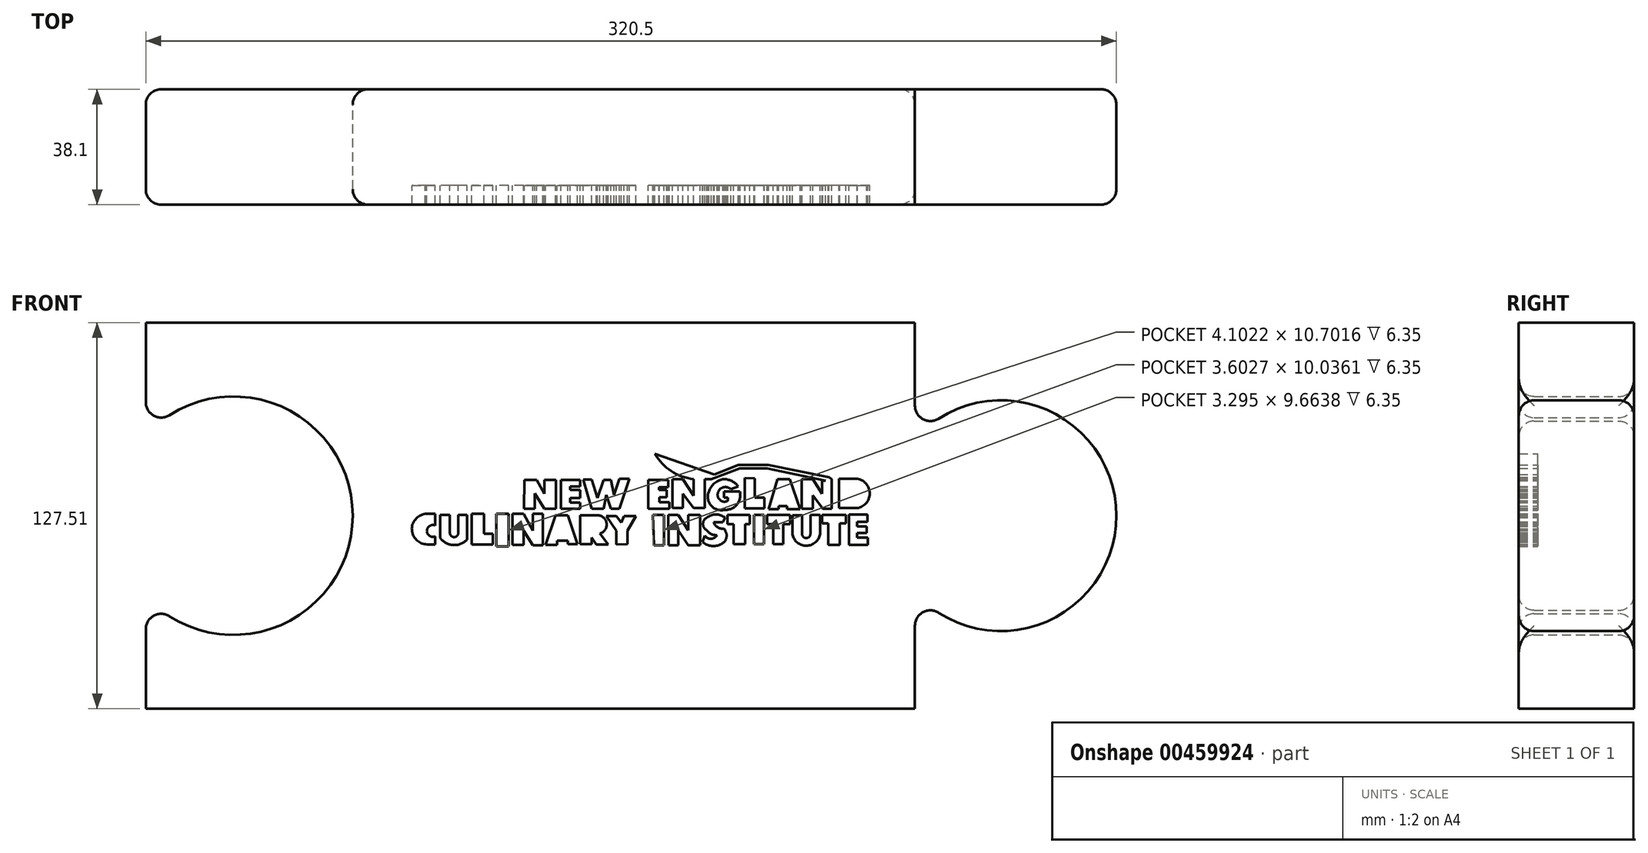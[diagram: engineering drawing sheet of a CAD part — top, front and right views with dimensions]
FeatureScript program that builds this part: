
annotation { "Feature Type Name" : "Feature", "Feature Type Description" : "" }
export const myFeature = defineFeature(function(context is Context, id is Id, definition is map)
    precondition{}
    {
        {
            var Q0;
            Q0=qCreatedBy(makeId("Front.planeOp"),FACE);
            var sketch = newSketch(context, id + "F0", { "sketchPlane" : qUnion([Q0])});
            skLineSegment(sketch, "E0", {"start": v(-171.41, 87.34) * mm, "end": v(82.59, 87.34) * mm});
            skLineSegment(sketch, "E1", {"start": v(-171.41, -40.17) * mm, "end": v(82.59, -40.17) * mm});
            skArc(sketch, "E2", {"start": v(82.59, -1.81) * mm, "mid": v(149.09, 23.59) * mm, "end": v(82.59, 48.99) * mm});
            skLineSegment(sketch, "E3", {"start": v(82.59, 48.99) * mm, "end": v(82.59, 87.34) * mm});
            skLineSegment(sketch, "E4", {"start": v(82.59, -1.81) * mm, "end": v(82.59, -40.17) * mm});
            skArc(sketch, "E5", {"start": v(-171.41, -3.08) * mm, "mid": v(-103.08, 23.59) * mm, "end": v(-171.41, 50.26) * mm});
            skLineSegment(sketch, "E6", {"start": v(-171.41, -3.08) * mm, "end": v(-171.41, -40.17) * mm});
            skLineSegment(sketch, "E7", {"start": v(-171.41, 50.26) * mm, "end": v(-171.41, 87.34) * mm});
            skLineSegment(sketch, "E8", {"start": v(-3.33, 44.08) * mm, "end": v(16.32, 37.2) * mm});
            skArc(sketch, "E9", {"start": v(-3.33, 44.08) * mm, "mid": v(2.1, 38.34) * mm, "end": v(9.53, 35.67) * mm});
            skLineSegment(sketch, "E10", {"start": v(9.53, 35.67) * mm, "end": v(9.53, 30.22) * mm});
            skLineSegment(sketch, "E11", {"start": v(9.53, 30.22) * mm, "end": v(5.93, 35.67) * mm});
            skLineSegment(sketch, "E12", {"start": v(5.93, 35.67) * mm, "end": v(2.47, 35.67) * mm});
            skLineSegment(sketch, "E13", {"start": v(2.47, 35.67) * mm, "end": v(2.47, 26.11) * mm});
            skLineSegment(sketch, "E14", {"start": v(2.47, 26.11) * mm, "end": v(5.93, 26.11) * mm});
            skLineSegment(sketch, "E15", {"start": v(5.93, 26.11) * mm, "end": v(5.93, 30.86) * mm});
            skLineSegment(sketch, "E16", {"start": v(5.93, 30.86) * mm, "end": v(9.53, 26.11) * mm});
            skLineSegment(sketch, "E17", {"start": v(9.53, 26.11) * mm, "end": v(13.12, 26.11) * mm});
            skLineSegment(sketch, "E18", {"start": v(13.12, 26.11) * mm, "end": v(13.12, 35.67) * mm});
            skLineSegment(sketch, "E19", {"start": v(13.12, 35.67) * mm, "end": v(15.3, 35.67) * mm});
            skLineSegment(sketch, "E20", {"start": v(16.32, 37.2) * mm, "end": v(24.18, 40.36) * mm});
            skLineSegment(sketch, "E21", {"start": v(15.3, 35.67) * mm, "end": v(24.7, 39.18) * mm});
            skLineSegment(sketch, "E22", {"start": v(24.7, 39.18) * mm, "end": v(33.7, 39.18) * mm});
            skLineSegment(sketch, "E23", {"start": v(24.18, 40.36) * mm, "end": v(34.15, 40.36) * mm});
            skLineSegment(sketch, "E24", {"start": v(33.7, 39.18) * mm, "end": v(53.02, 35.17) * mm});
            skLineSegment(sketch, "E25", {"start": v(34.15, 40.36) * mm, "end": v(54.26, 36.28) * mm});
            skLineSegment(sketch, "E26", {"start": v(53.02, 35.17) * mm, "end": v(51.9, 35.17) * mm});
            skLineSegment(sketch, "E27", {"start": v(51.9, 35.17) * mm, "end": v(51.9, 30.86) * mm});
            skLineSegment(sketch, "E28", {"start": v(51.9, 30.86) * mm, "end": v(48.82, 35.67) * mm});
            skLineSegment(sketch, "E29", {"start": v(48.82, 35.67) * mm, "end": v(45.2, 35.67) * mm});
            skLineSegment(sketch, "E30", {"start": v(45.2, 35.67) * mm, "end": v(45.2, 25.85) * mm});
            skLineSegment(sketch, "E31", {"start": v(45.2, 25.85) * mm, "end": v(48.89, 25.85) * mm});
            skLineSegment(sketch, "E32", {"start": v(48.89, 25.85) * mm, "end": v(48.89, 30.3) * mm});
            skLineSegment(sketch, "E33", {"start": v(48.89, 30.3) * mm, "end": v(52.16, 25.85) * mm});
            skLineSegment(sketch, "E34", {"start": v(52.16, 25.85) * mm, "end": v(55.07, 25.85) * mm});
            skLineSegment(sketch, "E35", {"start": v(55.07, 25.85) * mm, "end": v(55.07, 35.67) * mm});
            skLineSegment(sketch, "E36", {"start": v(54.26, 36.28) * mm, "end": v(55.07, 35.67) * mm});
            skLineSegment(sketch, "E37", {"start": v(-46.5, 25.85) * mm, "end": v(-42.9, 25.85) * mm});
            skLineSegment(sketch, "E38", {"start": v(-42.9, 25.85) * mm, "end": v(-42.9, 30.97) * mm});
            skLineSegment(sketch, "E39", {"start": v(-42.9, 30.97) * mm, "end": v(-39.72, 25.85) * mm});
            skLineSegment(sketch, "E40", {"start": v(-39.72, 25.85) * mm, "end": v(-35.95, 25.85) * mm});
            skLineSegment(sketch, "E41", {"start": v(-35.95, 25.85) * mm, "end": v(-35.95, 35.4) * mm});
            skLineSegment(sketch, "E42", {"start": v(-35.95, 35.4) * mm, "end": v(-39.72, 35.4) * mm});
            skLineSegment(sketch, "E43", {"start": v(-39.72, 35.4) * mm, "end": v(-39.72, 30.89) * mm});
            skLineSegment(sketch, "E44", {"start": v(-39.72, 30.89) * mm, "end": v(-42.33, 35.4) * mm});
            skLineSegment(sketch, "E45", {"start": v(-42.33, 35.4) * mm, "end": v(-46.4, 35.4) * mm});
            skLineSegment(sketch, "E46", {"start": v(-46.4, 35.4) * mm, "end": v(-46.5, 25.85) * mm});
            skLineSegment(sketch, "E47", {"start": v(-34.35, 35.4) * mm, "end": v(-34.35, 25.85) * mm});
            skLineSegment(sketch, "E48", {"start": v(-34.35, 25.85) * mm, "end": v(-27.92, 25.85) * mm});
            skLineSegment(sketch, "E49", {"start": v(-27.92, 25.85) * mm, "end": v(-27.92, 27.95) * mm});
            skLineSegment(sketch, "E50", {"start": v(-27.92, 27.95) * mm, "end": v(-31.2, 27.95) * mm});
            skLineSegment(sketch, "E51", {"start": v(-31.2, 27.95) * mm, "end": v(-31.2, 29.39) * mm});
            skLineSegment(sketch, "E52", {"start": v(-31.2, 29.39) * mm, "end": v(-27.92, 29.39) * mm});
            skLineSegment(sketch, "E53", {"start": v(-27.92, 29.39) * mm, "end": v(-27.92, 32.14) * mm});
            skLineSegment(sketch, "E54", {"start": v(-27.92, 32.14) * mm, "end": v(-31.2, 32.14) * mm});
            skLineSegment(sketch, "E55", {"start": v(-31.2, 32.14) * mm, "end": v(-31.2, 33.29) * mm});
            skLineSegment(sketch, "E56", {"start": v(-31.2, 33.29) * mm, "end": v(-27.92, 33.29) * mm});
            skLineSegment(sketch, "E57", {"start": v(-27.92, 35.4) * mm, "end": v(-34.35, 35.4) * mm});
            skLineSegment(sketch, "E58", {"start": v(-24.13, 25.85) * mm, "end": v(-20.2, 25.85) * mm});
            skLineSegment(sketch, "E59", {"start": v(-26.97, 35.48) * mm, "end": v(-24.13, 35.48) * mm});
            skLineSegment(sketch, "E60", {"start": v(-24.13, 35.48) * mm, "end": v(-22.3, 29.39) * mm});
            skLineSegment(sketch, "E61", {"start": v(-22.3, 29.39) * mm, "end": v(-20.2, 35.4) * mm});
            skLineSegment(sketch, "E62", {"start": v(-20.2, 35.4) * mm, "end": v(-17.84, 35.4) * mm});
            skLineSegment(sketch, "E63", {"start": v(-27.92, 35.4) * mm, "end": v(-27.92, 33.29) * mm});
            skLineSegment(sketch, "E64", {"start": v(-26.97, 35.48) * mm, "end": v(-24.13, 25.85) * mm});
            skLineSegment(sketch, "E65", {"start": v(-17.84, 35.4) * mm, "end": v(-16.74, 30.44) * mm});
            skLineSegment(sketch, "E66", {"start": v(-16.74, 30.44) * mm, "end": v(-14.96, 35.82) * mm});
            skLineSegment(sketch, "E67", {"start": v(-14.96, 35.82) * mm, "end": v(-11.7, 35.82) * mm});
            skLineSegment(sketch, "E68", {"start": v(-20.2, 25.85) * mm, "end": v(-19.33, 30.44) * mm});
            skLineSegment(sketch, "E69", {"start": v(-19.33, 30.44) * mm, "end": v(-17.84, 25.85) * mm});
            skLineSegment(sketch, "E70", {"start": v(-17.84, 25.85) * mm, "end": v(-14.96, 25.85) * mm});
            skLineSegment(sketch, "E71", {"start": v(-14.96, 25.85) * mm, "end": v(-11.7, 35.82) * mm});
            skLineSegment(sketch, "E72", {"start": v(-5.47, 35.4) * mm, "end": v(-5.47, 25.85) * mm});
            skLineSegment(sketch, "E73", {"start": v(-5.47, 25.85) * mm, "end": v(1.5, 25.85) * mm});
            skLineSegment(sketch, "E74", {"start": v(1.5, 25.85) * mm, "end": v(1.5, 28.1) * mm});
            skLineSegment(sketch, "E75", {"start": v(1.5, 28.1) * mm, "end": v(-1.81, 28.1) * mm});
            skLineSegment(sketch, "E76", {"start": v(-1.81, 28.1) * mm, "end": v(-1.81, 29.65) * mm});
            skLineSegment(sketch, "E77", {"start": v(-1.81, 29.65) * mm, "end": v(0.62, 29.65) * mm});
            skLineSegment(sketch, "E78", {"start": v(-5.47, 35.4) * mm, "end": v(1.18, 35.4) * mm});
            skLineSegment(sketch, "E79", {"start": v(1.18, 35.4) * mm, "end": v(1.18, 32.97) * mm});
            skLineSegment(sketch, "E80", {"start": v(1.5, 32.97) * mm, "end": v(-1.93, 32.97) * mm});
            skLineSegment(sketch, "E81", {"start": v(-1.93, 32.97) * mm, "end": v(-1.93, 32.08) * mm});
            skLineSegment(sketch, "E82", {"start": v(-1.93, 32.08) * mm, "end": v(0.62, 32.08) * mm});
            skPoint(sketch, "E83.orphan", {"position": v(1.5, 29.65) * mm});
            skLineSegment(sketch, "E84", {"start": v(0.62, 32.08) * mm, "end": v(0.62, 29.65) * mm});
            skLineSegment(sketch, "E85", {"start": v(26.33, 36.01) * mm, "end": v(26.33, 26.06) * mm});
            skLineSegment(sketch, "E86", {"start": v(26.33, 26.06) * mm, "end": v(32.9, 26.06) * mm});
            skLineSegment(sketch, "E87", {"start": v(32.9, 26.06) * mm, "end": v(32.9, 29.5) * mm});
            skLineSegment(sketch, "E88", {"start": v(32.9, 29.5) * mm, "end": v(29.73, 29.5) * mm});
            skLineSegment(sketch, "E89", {"start": v(29.73, 29.5) * mm, "end": v(29.73, 35.89) * mm});
            skLineSegment(sketch, "E90", {"start": v(29.73, 35.89) * mm, "end": v(26.33, 36.01) * mm});
            skLineSegment(sketch, "E91", {"start": v(21.76, 32.34) * mm, "end": v(24.25, 33.27) * mm});
            skLineSegment(sketch, "E92", {"start": v(19.48, 29.52) * mm, "end": v(20.8, 29.52) * mm});
            skLineSegment(sketch, "E93", {"start": v(20.8, 29.52) * mm, "end": v(20.8, 28.5) * mm});
            skLineSegment(sketch, "E94", {"start": v(19.48, 29.52) * mm, "end": v(19.48, 31.58) * mm});
            skLineSegment(sketch, "E95", {"start": v(19.48, 31.58) * mm, "end": v(24.75, 31.58) * mm});
            skArc(sketch, "E96", {"start": v(19.64, 25.53) * mm, "mid": v(23.77, 27.23) * mm, "end": v(24.75, 31.58) * mm});
            skArc(sketch, "E97", {"start": v(14.53, 31.58) * mm, "mid": v(15.21, 26.98) * mm, "end": v(19.64, 25.53) * mm});
            skArc(sketch, "E98", {"start": v(17.48, 30.99) * mm, "mid": v(18.33, 28.66) * mm, "end": v(20.8, 28.5) * mm});
            skArc(sketch, "E99", {"start": v(21.76, 32.34) * mm, "mid": v(19.22, 32.94) * mm, "end": v(17.48, 30.99) * mm});
            skLineSegment(sketch, "E100", {"start": v(34.22, 25.8) * mm, "end": v(37.57, 25.8) * mm});
            skLineSegment(sketch, "E101", {"start": v(34.22, 25.8) * mm, "end": v(37.24, 35.7) * mm});
            skLineSegment(sketch, "E102", {"start": v(37.24, 35.7) * mm, "end": v(41.29, 35.7) * mm});
            skLineSegment(sketch, "E103", {"start": v(41.29, 35.7) * mm, "end": v(44.73, 25.8) * mm});
            skLineSegment(sketch, "E104", {"start": v(44.73, 25.8) * mm, "end": v(40.37, 25.8) * mm});
            skLineSegment(sketch, "E105", {"start": v(40.37, 25.8) * mm, "end": v(40.37, 26.82) * mm});
            skLineSegment(sketch, "E106", {"start": v(40.37, 26.82) * mm, "end": v(37.57, 26.82) * mm});
            skLineSegment(sketch, "E107", {"start": v(37.57, 26.82) * mm, "end": v(37.57, 25.8) * mm});
            skLineSegment(sketch, "E108", {"start": v(39.29, 31.76) * mm, "end": v(38.79, 29.4) * mm});
            skLineSegment(sketch, "E109", {"start": v(38.79, 29.4) * mm, "end": v(40, 29.4) * mm});
            skLineSegment(sketch, "E110", {"start": v(39.29, 31.76) * mm, "end": v(40, 29.4) * mm});
            skLineSegment(sketch, "E111", {"start": v(57.55, 35.85) * mm, "end": v(57.55, 26.08) * mm});
            skLineSegment(sketch, "E112", {"start": v(57.55, 26.08) * mm, "end": v(63.6, 26.08) * mm});
            skLineSegment(sketch, "E113", {"start": v(57.55, 35.85) * mm, "end": v(62.73, 35.85) * mm});
            skLineSegment(sketch, "E114", {"start": v(60.73, 32.8) * mm, "end": v(60.73, 29.4) * mm});
            skArc(sketch, "E115", {"start": v(60.73, 29.4) * mm, "mid": v(63.48, 31.1) * mm, "end": v(60.73, 32.8) * mm});
            skArc(sketch, "E116", {"start": v(63.6, 26.08) * mm, "mid": v(67.63, 31.36) * mm, "end": v(62.73, 35.85) * mm});
            skArc(sketch, "E117", {"start": v(19.64, 35.67) * mm, "mid": v(16.48, 34.38) * mm, "end": v(14.53, 31.58) * mm});
            skArc(sketch, "E118", {"start": v(24.25, 33.27) * mm, "mid": v(22.2, 34.96) * mm, "end": v(19.64, 35.67) * mm});
            skLineSegment(sketch, "E119", {"start": v(-75.8, 24.17) * mm, "end": v(-75.8, 20.33) * mm});
            skLineSegment(sketch, "E120", {"start": v(-75.8, 24.17) * mm, "end": v(-79.12, 24.17) * mm});
            skLineSegment(sketch, "E121", {"start": v(-75.8, 16.76) * mm, "end": v(-75.8, 14.1) * mm});
            skLineSegment(sketch, "E122", {"start": v(-75.8, 14.1) * mm, "end": v(-78.47, 14.1) * mm});
            skArc(sketch, "E123", {"start": v(-79.12, 24.17) * mm, "mid": v(-83.52, 18.83) * mm, "end": v(-78.47, 14.1) * mm});
            skArc(sketch, "E124", {"start": v(-75.8, 20.33) * mm, "mid": v(-78.57, 18.55) * mm, "end": v(-75.8, 16.76) * mm});
            skLineSegment(sketch, "E125", {"start": v(-63.75, 24.17) * mm, "end": v(-63.75, 14.1) * mm});
            skLineSegment(sketch, "E126", {"start": v(-63.75, 14.1) * mm, "end": v(-56.8, 14.1) * mm});
            skLineSegment(sketch, "E127", {"start": v(-56.8, 14.1) * mm, "end": v(-56.8, 17.57) * mm});
            skLineSegment(sketch, "E128", {"start": v(-56.8, 17.57) * mm, "end": v(-59.73, 17.57) * mm});
            skLineSegment(sketch, "E129", {"start": v(-59.73, 17.57) * mm, "end": v(-59.73, 24.17) * mm});
            skLineSegment(sketch, "E130", {"start": v(-59.73, 24.17) * mm, "end": v(-63.75, 24.17) * mm});
            skLineSegment(sketch, "E131", {"start": v(-55.7, 24.17) * mm, "end": v(-55.7, 13.47) * mm});
            skLineSegment(sketch, "E132", {"start": v(-55.7, 13.47) * mm, "end": v(-51.6, 13.47) * mm});
            skLineSegment(sketch, "E133", {"start": v(-51.6, 13.47) * mm, "end": v(-51.6, 24.17) * mm});
            skLineSegment(sketch, "E134", {"start": v(-55.7, 24.17) * mm, "end": v(-51.6, 24.17) * mm});
            skLineSegment(sketch, "E135", {"start": v(-74.2, 23.79) * mm, "end": v(-70.98, 23.79) * mm});
            skLineSegment(sketch, "E136", {"start": v(-70.98, 23.79) * mm, "end": v(-70.98, 18.01) * mm});
            skLineSegment(sketch, "E137", {"start": v(-68.18, 23.79) * mm, "end": v(-65.3, 23.79) * mm});
            skLineSegment(sketch, "E138", {"start": v(-68.18, 23.79) * mm, "end": v(-68.18, 17.92) * mm});
            skLineSegment(sketch, "E139", {"start": v(-65.3, 23.79) * mm, "end": v(-65.3, 15.65) * mm});
            skLineSegment(sketch, "E140", {"start": v(-74.2, 23.79) * mm, "end": v(-74.2, 16.23) * mm});
            skArc(sketch, "E141", {"start": v(-70.98, 18.01) * mm, "mid": v(-69.63, 16.52) * mm, "end": v(-68.18, 17.92) * mm});
            skArc(sketch, "E142", {"start": v(-74.2, 16.23) * mm, "mid": v(-69.88, 13.89) * mm, "end": v(-65.3, 15.65) * mm});
            skLineSegment(sketch, "E143", {"start": v(-50.26, 13.96) * mm, "end": v(-46.65, 13.96) * mm});
            skLineSegment(sketch, "E144", {"start": v(-46.65, 13.96) * mm, "end": v(-46.65, 18.66) * mm});
            skLineSegment(sketch, "E145", {"start": v(-46.65, 18.66) * mm, "end": v(-43.63, 13.8) * mm});
            skLineSegment(sketch, "E146", {"start": v(-43.63, 13.8) * mm, "end": v(-40.28, 13.8) * mm});
            skLineSegment(sketch, "E147", {"start": v(-40.28, 13.8) * mm, "end": v(-40.28, 24.17) * mm});
            skLineSegment(sketch, "E148", {"start": v(-40.28, 24.17) * mm, "end": v(-43.63, 24.17) * mm});
            skLineSegment(sketch, "E149", {"start": v(-43.63, 24.17) * mm, "end": v(-43.63, 18.66) * mm});
            skLineSegment(sketch, "E150", {"start": v(-43.63, 18.66) * mm, "end": v(-46.65, 24.17) * mm});
            skLineSegment(sketch, "E151", {"start": v(-50.26, 13.96) * mm, "end": v(-50.26, 24.28) * mm});
            skLineSegment(sketch, "E152", {"start": v(-50.26, 24.28) * mm, "end": v(-46.65, 24.17) * mm});
            skLineSegment(sketch, "E153", {"start": v(-35.11, 17.5) * mm, "end": v(-33.2, 17.5) * mm});
            skLineSegment(sketch, "E154", {"start": v(-33.2, 17.5) * mm, "end": v(-34.16, 20.17) * mm});
            skLineSegment(sketch, "E155", {"start": v(-34.16, 20.17) * mm, "end": v(-35.11, 17.5) * mm});
            skLineSegment(sketch, "E156", {"start": v(-35.62, 15.4) * mm, "end": v(-35.62, 13.94) * mm});
            skLineSegment(sketch, "E157", {"start": v(-35.62, 13.94) * mm, "end": v(-39.39, 13.94) * mm});
            skLineSegment(sketch, "E158", {"start": v(-39.39, 13.94) * mm, "end": v(-36.12, 23.74) * mm});
            skLineSegment(sketch, "E159", {"start": v(-36.12, 23.74) * mm, "end": v(-32, 23.74) * mm});
            skLineSegment(sketch, "E160", {"start": v(-32, 23.74) * mm, "end": v(-28.88, 14.19) * mm});
            skLineSegment(sketch, "E161", {"start": v(-28.88, 14.19) * mm, "end": v(-32, 14.19) * mm});
            skLineSegment(sketch, "E162", {"start": v(-32, 14.19) * mm, "end": v(-32, 15.34) * mm});
            skLineSegment(sketch, "E163", {"start": v(-32, 15.34) * mm, "end": v(-35.62, 15.4) * mm});
            skLineSegment(sketch, "E164", {"start": v(-15.98, 18.61) * mm, "end": v(-19.36, 23.46) * mm});
            skLineSegment(sketch, "E165", {"start": v(-19.36, 23.46) * mm, "end": v(-16.07, 23.46) * mm});
            skLineSegment(sketch, "E166", {"start": v(-16.07, 23.46) * mm, "end": v(-14.38, 21.33) * mm});
            skLineSegment(sketch, "E167", {"start": v(-14.38, 21.33) * mm, "end": v(-13.42, 23.46) * mm});
            skLineSegment(sketch, "E168", {"start": v(-13.42, 23.46) * mm, "end": v(-9.49, 23.46) * mm});
            skLineSegment(sketch, "E169", {"start": v(-9.49, 23.46) * mm, "end": v(-12.32, 18.7) * mm});
            skLineSegment(sketch, "E170", {"start": v(-12.32, 18.7) * mm, "end": v(-12.32, 14.22) * mm});
            skLineSegment(sketch, "E171", {"start": v(-15.98, 18.61) * mm, "end": v(-15.98, 14.13) * mm});
            skLineSegment(sketch, "E172", {"start": v(-15.98, 14.13) * mm, "end": v(-12.32, 14.22) * mm});
            skLineSegment(sketch, "E173", {"start": v(-24.13, 16.33) * mm, "end": v(-24.13, 14.22) * mm});
            skLineSegment(sketch, "E174", {"start": v(-24.13, 14.22) * mm, "end": v(-27.92, 14.22) * mm});
            skLineSegment(sketch, "E175", {"start": v(-27.92, 14.22) * mm, "end": v(-27.92, 23.73) * mm});
            skLineSegment(sketch, "E176", {"start": v(-27.92, 23.73) * mm, "end": v(-22.3, 23.73) * mm});
            skLineSegment(sketch, "E177", {"start": v(-24.13, 16.33) * mm, "end": v(-22.66, 14.13) * mm});
            skLineSegment(sketch, "E178", {"start": v(-22.66, 14.13) * mm, "end": v(-18.63, 14.13) * mm});
            skLineSegment(sketch, "E179", {"start": v(-18.63, 14.13) * mm, "end": v(-21.47, 17.7) * mm});
            skLineSegment(sketch, "E180", {"start": v(-24.13, 21.17) * mm, "end": v(-24.13, 19.62) * mm});
            skArc(sketch, "E181", {"start": v(-24.13, 19.62) * mm, "mid": v(-22.7, 20.4) * mm, "end": v(-24.13, 21.17) * mm});
            skArc(sketch, "E182", {"start": v(-21.47, 17.7) * mm, "mid": v(-19.25, 21.08) * mm, "end": v(-22.3, 23.73) * mm});
            skLineSegment(sketch, "E183", {"start": v(-3.58, 13.82) * mm, "end": v(-0.33, 13.82) * mm});
            skLineSegment(sketch, "E184", {"start": v(-0.33, 13.82) * mm, "end": v(-0.33, 23.85) * mm});
            skLineSegment(sketch, "E185", {"start": v(-0.33, 23.85) * mm, "end": v(-3.93, 23.85) * mm});
            skLineSegment(sketch, "E186", {"start": v(-3.93, 23.85) * mm, "end": v(-3.58, 13.82) * mm});
            skLineSegment(sketch, "E187", {"start": v(1.3, 13.82) * mm, "end": v(4.4, 13.82) * mm});
            skLineSegment(sketch, "E188", {"start": v(4.4, 13.82) * mm, "end": v(4.4, 18.8) * mm});
            skLineSegment(sketch, "E189", {"start": v(4.4, 18.8) * mm, "end": v(7.74, 13.82) * mm});
            skLineSegment(sketch, "E190", {"start": v(7.74, 13.82) * mm, "end": v(11.68, 13.82) * mm});
            skLineSegment(sketch, "E191", {"start": v(11.68, 13.82) * mm, "end": v(11.68, 23.85) * mm});
            skLineSegment(sketch, "E192", {"start": v(11.68, 23.85) * mm, "end": v(7.74, 23.85) * mm});
            skLineSegment(sketch, "E193", {"start": v(7.74, 23.85) * mm, "end": v(7.74, 18.8) * mm});
            skLineSegment(sketch, "E194", {"start": v(7.74, 18.8) * mm, "end": v(4.4, 23.85) * mm});
            skLineSegment(sketch, "E195", {"start": v(4.4, 23.85) * mm, "end": v(1.13, 23.85) * mm});
            skLineSegment(sketch, "E196", {"start": v(1.13, 23.85) * mm, "end": v(1.3, 13.82) * mm});
            skLineSegment(sketch, "E197", {"start": v(20.7, 20.8) * mm, "end": v(22.74, 20.8) * mm});
            skLineSegment(sketch, "E198", {"start": v(22.74, 20.8) * mm, "end": v(22.74, 14.24) * mm});
            skLineSegment(sketch, "E199", {"start": v(22.74, 14.24) * mm, "end": v(26.5, 14.24) * mm});
            skLineSegment(sketch, "E200", {"start": v(26.5, 14.24) * mm, "end": v(26.5, 20.8) * mm});
            skLineSegment(sketch, "E201", {"start": v(26.5, 20.8) * mm, "end": v(28.08, 20.8) * mm});
            skLineSegment(sketch, "E202", {"start": v(28.08, 20.8) * mm, "end": v(28.08, 23.9) * mm});
            skLineSegment(sketch, "E203", {"start": v(28.08, 23.9) * mm, "end": v(20.7, 23.9) * mm});
            skLineSegment(sketch, "E204", {"start": v(20.7, 23.9) * mm, "end": v(20.7, 20.8) * mm});
            skLineSegment(sketch, "E205", {"start": v(29.45, 14.24) * mm, "end": v(32.74, 14.24) * mm});
            skLineSegment(sketch, "E206", {"start": v(32.74, 14.24) * mm, "end": v(32.74, 23.9) * mm});
            skLineSegment(sketch, "E207", {"start": v(32.74, 23.9) * mm, "end": v(29.45, 23.9) * mm});
            skLineSegment(sketch, "E208", {"start": v(29.45, 23.9) * mm, "end": v(29.45, 14.24) * mm});
            skLineSegment(sketch, "E209", {"start": v(35.8, 14.24) * mm, "end": v(39.1, 14.24) * mm});
            skLineSegment(sketch, "E210", {"start": v(39.1, 14.24) * mm, "end": v(39.1, 20.8) * mm});
            skLineSegment(sketch, "E211", {"start": v(39.1, 20.8) * mm, "end": v(41.38, 20.8) * mm});
            skLineSegment(sketch, "E212", {"start": v(41.38, 20.8) * mm, "end": v(41.38, 23.9) * mm});
            skLineSegment(sketch, "E213", {"start": v(41.38, 23.9) * mm, "end": v(33.76, 23.9) * mm});
            skLineSegment(sketch, "E214", {"start": v(33.76, 23.9) * mm, "end": v(33.76, 20.8) * mm});
            skLineSegment(sketch, "E215", {"start": v(33.76, 20.8) * mm, "end": v(35.73, 20.8) * mm});
            skLineSegment(sketch, "E216", {"start": v(35.73, 20.8) * mm, "end": v(35.8, 14.24) * mm});
            skLineSegment(sketch, "E217.bottom", {"start": v(60.74, 24.03) * mm, "end": v(63.44, 24.03) * mm});
            skLineSegment(sketch, "E217.top", {"start": v(60.74, 13.95) * mm, "end": v(63.44, 13.95) * mm});
            skLineSegment(sketch, "E217.left", {"start": v(60.74, 24.03) * mm, "end": v(60.74, 13.95) * mm});
            skLineSegment(sketch, "E217.right", {"start": v(63.44, 21.62) * mm, "end": v(63.44, 19.99) * mm});
            skLineSegment(sketch, "E218.bottom", {"start": v(67.07, 16.3) * mm, "end": v(63.44, 16.3) * mm});
            skLineSegment(sketch, "E218.top", {"start": v(67.07, 13.95) * mm, "end": v(63.44, 13.95) * mm});
            skLineSegment(sketch, "E218.left", {"start": v(67.07, 16.3) * mm, "end": v(67.07, 13.95) * mm});
            skLineSegment(sketch, "E219.bottom", {"start": v(66.71, 19.99) * mm, "end": v(63.44, 19.99) * mm});
            skLineSegment(sketch, "E219.top", {"start": v(66.71, 17.85) * mm, "end": v(63.44, 17.85) * mm});
            skLineSegment(sketch, "E219.left", {"start": v(66.71, 19.99) * mm, "end": v(66.71, 17.85) * mm});
            skLineSegment(sketch, "E220.bottom", {"start": v(66.85, 24.03) * mm, "end": v(63.44, 24.03) * mm});
            skLineSegment(sketch, "E220.top", {"start": v(66.85, 21.62) * mm, "end": v(63.44, 21.62) * mm});
            skLineSegment(sketch, "E220.left", {"start": v(66.85, 24.03) * mm, "end": v(66.85, 21.62) * mm});
            skLineSegment(sketch, "E220.right", {"start": v(63.44, 24.03) * mm, "end": v(63.44, 24.03) * mm});
            skLineSegment(sketch, "E221.trimOffspring", {"start": v(63.44, 17.85) * mm, "end": v(63.44, 16.3) * mm});
            skLineSegment(sketch, "E222.bottom", {"start": v(51.94, 23.8) * mm, "end": v(59.77, 23.8) * mm});
            skLineSegment(sketch, "E222.top", {"start": v(51.94, 21.09) * mm, "end": v(53.97, 21.09) * mm});
            skLineSegment(sketch, "E222.left", {"start": v(51.94, 23.8) * mm, "end": v(51.94, 21.09) * mm});
            skLineSegment(sketch, "E222.right", {"start": v(59.77, 23.8) * mm, "end": v(59.77, 21.09) * mm});
            skLineSegment(sketch, "E223.top", {"start": v(53.97, 13.9) * mm, "end": v(57.79, 13.9) * mm});
            skLineSegment(sketch, "E223.left", {"start": v(53.97, 21.09) * mm, "end": v(53.97, 13.9) * mm});
            skLineSegment(sketch, "E223.right", {"start": v(57.79, 21.09) * mm, "end": v(57.79, 13.9) * mm});
            skLineSegment(sketch, "E224.trimOffspring", {"start": v(57.79, 21.09) * mm, "end": v(59.77, 21.09) * mm});
            skLineSegment(sketch, "E225.bottom", {"start": v(42.13, 23.7) * mm, "end": v(45.36, 23.7) * mm});
            skLineSegment(sketch, "E225.left", {"start": v(42.13, 23.7) * mm, "end": v(42.13, 17.43) * mm});
            skLineSegment(sketch, "E225.right", {"start": v(45.36, 23.7) * mm, "end": v(45.36, 17.43) * mm});
            skLineSegment(sketch, "E226.bottom", {"start": v(48.04, 23.8) * mm, "end": v(51.28, 23.8) * mm});
            skLineSegment(sketch, "E226.left", {"start": v(48.04, 23.8) * mm, "end": v(48.04, 17.53) * mm});
            skLineSegment(sketch, "E226.right", {"start": v(51.28, 23.8) * mm, "end": v(51.28, 17.53) * mm});
            skArc(sketch, "E227", {"start": v(45.36, 17.43) * mm, "mid": v(46.75, 16.18) * mm, "end": v(48.04, 17.53) * mm});
            skArc(sketch, "E228", {"start": v(42.13, 17.43) * mm, "mid": v(46.74, 13.67) * mm, "end": v(51.28, 17.53) * mm});
            skLineSegment(sketch, "E229", {"start": v(12.46, 14.9) * mm, "end": v(13.22, 16.94) * mm});
            skLineSegment(sketch, "E230", {"start": v(19.18, 21.38) * mm, "end": v(19.88, 22.9) * mm});
            skArc(sketch, "E231", {"start": v(19.88, 22.9) * mm, "mid": v(16.87, 24) * mm, "end": v(13.86, 22.9) * mm});
            skArc(sketch, "E232", {"start": v(13.86, 22.9) * mm, "mid": v(12.6, 20.85) * mm, "end": v(13.86, 18.8) * mm});
            skArc(sketch, "E233", {"start": v(13.86, 18.8) * mm, "mid": v(15.33, 17.52) * mm, "end": v(17.25, 17.17) * mm});
            skArc(sketch, "E234", {"start": v(13.22, 16.94) * mm, "mid": v(15.3, 15.96) * mm, "end": v(17.25, 17.17) * mm});
            skLineSegment(sketch, "E235", {"start": v(19.18, 21.38) * mm, "end": v(16.14, 21.38) * mm});
            skArc(sketch, "E236", {"start": v(16.14, 21.38) * mm, "mid": v(17.45, 19.77) * mm, "end": v(19.47, 19.28) * mm});
            skArc(sketch, "E237", {"start": v(18.07, 13.96) * mm, "mid": v(20.3, 16.21) * mm, "end": v(19.47, 19.28) * mm});
            skArc(sketch, "E238", {"start": v(12.46, 14.9) * mm, "mid": v(15.13, 13.62) * mm, "end": v(18.07, 13.96) * mm});
            skSolve(sketch);
        }
        {
            var Q0;
            Q0 = qSketchRegion(id + "F0", true);
            extrude(context, id + "F1", {"entities" : qUnion([Q0]), "depth" : 38.1 * mm});
        }
        {
            var Q0;
            Q0=makeQuery(id+"F1.opExtrude","CAP_FACE",FACE,{"disambiguationData":[OSD([sQuery(id+"F0.wireOp",EDGE,"E0"),sQuery(id+"F0.wireOp",EDGE,"E1"),sQuery(id+"F0.wireOp",EDGE,"E2"),sQuery(id+"F0.wireOp",EDGE,"E3"),sQuery(id+"F0.wireOp",EDGE,"E4"),sQuery(id+"F0.wireOp",EDGE,"E5"),sQuery(id+"F0.wireOp",EDGE,"E6"),sQuery(id+"F0.wireOp",EDGE,"E7"),sQuery(id+"F0.wireOp",EDGE,"E8"),sQuery(id+"F0.wireOp",EDGE,"E9"),sQuery(id+"F0.wireOp",EDGE,"E10"),sQuery(id+"F0.wireOp",EDGE,"E11"),sQuery(id+"F0.wireOp",EDGE,"E12"),sQuery(id+"F0.wireOp",EDGE,"E13"),sQuery(id+"F0.wireOp",EDGE,"E14"),sQuery(id+"F0.wireOp",EDGE,"E15"),sQuery(id+"F0.wireOp",EDGE,"E16"),sQuery(id+"F0.wireOp",EDGE,"E17"),sQuery(id+"F0.wireOp",EDGE,"E18"),sQuery(id+"F0.wireOp",EDGE,"E19"),sQuery(id+"F0.wireOp",EDGE,"E20"),sQuery(id+"F0.wireOp",EDGE,"E21"),sQuery(id+"F0.wireOp",EDGE,"E22"),sQuery(id+"F0.wireOp",EDGE,"E23"),sQuery(id+"F0.wireOp",EDGE,"E24"),sQuery(id+"F0.wireOp",EDGE,"E25"),sQuery(id+"F0.wireOp",EDGE,"E26"),sQuery(id+"F0.wireOp",EDGE,"E27"),sQuery(id+"F0.wireOp",EDGE,"E28"),sQuery(id+"F0.wireOp",EDGE,"E29"),sQuery(id+"F0.wireOp",EDGE,"E30"),sQuery(id+"F0.wireOp",EDGE,"E31"),sQuery(id+"F0.wireOp",EDGE,"E32"),sQuery(id+"F0.wireOp",EDGE,"E33"),sQuery(id+"F0.wireOp",EDGE,"E34"),sQuery(id+"F0.wireOp",EDGE,"E35"),sQuery(id+"F0.wireOp",EDGE,"E36"),sQuery(id+"F0.wireOp",EDGE,"E37"),sQuery(id+"F0.wireOp",EDGE,"E38"),sQuery(id+"F0.wireOp",EDGE,"E39"),sQuery(id+"F0.wireOp",EDGE,"E40"),sQuery(id+"F0.wireOp",EDGE,"E41"),sQuery(id+"F0.wireOp",EDGE,"E42"),sQuery(id+"F0.wireOp",EDGE,"E43"),sQuery(id+"F0.wireOp",EDGE,"E44"),sQuery(id+"F0.wireOp",EDGE,"E45"),sQuery(id+"F0.wireOp",EDGE,"E46"),sQuery(id+"F0.wireOp",EDGE,"E47"),sQuery(id+"F0.wireOp",EDGE,"E48"),sQuery(id+"F0.wireOp",EDGE,"E49"),sQuery(id+"F0.wireOp",EDGE,"E50"),sQuery(id+"F0.wireOp",EDGE,"E51"),sQuery(id+"F0.wireOp",EDGE,"E52"),sQuery(id+"F0.wireOp",EDGE,"E53"),sQuery(id+"F0.wireOp",EDGE,"E54"),sQuery(id+"F0.wireOp",EDGE,"E55"),sQuery(id+"F0.wireOp",EDGE,"E56"),sQuery(id+"F0.wireOp",EDGE,"E57"),sQuery(id+"F0.wireOp",EDGE,"E58"),sQuery(id+"F0.wireOp",EDGE,"E59"),sQuery(id+"F0.wireOp",EDGE,"E60"),sQuery(id+"F0.wireOp",EDGE,"E61"),sQuery(id+"F0.wireOp",EDGE,"E62"),sQuery(id+"F0.wireOp",EDGE,"E63"),sQuery(id+"F0.wireOp",EDGE,"E64"),sQuery(id+"F0.wireOp",EDGE,"E65"),sQuery(id+"F0.wireOp",EDGE,"E66"),sQuery(id+"F0.wireOp",EDGE,"E67"),sQuery(id+"F0.wireOp",EDGE,"E68"),sQuery(id+"F0.wireOp",EDGE,"E69"),sQuery(id+"F0.wireOp",EDGE,"E70"),sQuery(id+"F0.wireOp",EDGE,"E71"),sQuery(id+"F0.wireOp",EDGE,"E72"),sQuery(id+"F0.wireOp",EDGE,"E73"),sQuery(id+"F0.wireOp",EDGE,"E74"),sQuery(id+"F0.wireOp",EDGE,"E75"),sQuery(id+"F0.wireOp",EDGE,"E76"),sQuery(id+"F0.wireOp",EDGE,"E77"),sQuery(id+"F0.wireOp",EDGE,"E78"),sQuery(id+"F0.wireOp",EDGE,"E79"),sQuery(id+"F0.wireOp",EDGE,"E80"),sQuery(id+"F0.wireOp",EDGE,"E81"),sQuery(id+"F0.wireOp",EDGE,"E82"),sQuery(id+"F0.wireOp",EDGE,"E84"),sQuery(id+"F0.wireOp",EDGE,"E85"),sQuery(id+"F0.wireOp",EDGE,"E86"),sQuery(id+"F0.wireOp",EDGE,"E87"),sQuery(id+"F0.wireOp",EDGE,"E88"),sQuery(id+"F0.wireOp",EDGE,"E89"),sQuery(id+"F0.wireOp",EDGE,"E90"),sQuery(id+"F0.wireOp",EDGE,"E91"),sQuery(id+"F0.wireOp",EDGE,"E92"),sQuery(id+"F0.wireOp",EDGE,"E93"),sQuery(id+"F0.wireOp",EDGE,"E94"),sQuery(id+"F0.wireOp",EDGE,"E95"),sQuery(id+"F0.wireOp",EDGE,"E96"),sQuery(id+"F0.wireOp",EDGE,"E97"),sQuery(id+"F0.wireOp",EDGE,"E98"),sQuery(id+"F0.wireOp",EDGE,"E99"),sQuery(id+"F0.wireOp",EDGE,"E100"),sQuery(id+"F0.wireOp",EDGE,"E101"),sQuery(id+"F0.wireOp",EDGE,"E102"),sQuery(id+"F0.wireOp",EDGE,"E103"),sQuery(id+"F0.wireOp",EDGE,"E104"),sQuery(id+"F0.wireOp",EDGE,"E105"),sQuery(id+"F0.wireOp",EDGE,"E106"),sQuery(id+"F0.wireOp",EDGE,"E107"),sQuery(id+"F0.wireOp",EDGE,"E111"),sQuery(id+"F0.wireOp",EDGE,"E112"),sQuery(id+"F0.wireOp",EDGE,"E113"),sQuery(id+"F0.wireOp",EDGE,"E116"),sQuery(id+"F0.wireOp",EDGE,"E117"),sQuery(id+"F0.wireOp",EDGE,"E118"),sQuery(id+"F0.wireOp",EDGE,"E119"),sQuery(id+"F0.wireOp",EDGE,"E120"),sQuery(id+"F0.wireOp",EDGE,"E121"),sQuery(id+"F0.wireOp",EDGE,"E122"),sQuery(id+"F0.wireOp",EDGE,"E123"),sQuery(id+"F0.wireOp",EDGE,"E124"),sQuery(id+"F0.wireOp",EDGE,"E125"),sQuery(id+"F0.wireOp",EDGE,"E126"),sQuery(id+"F0.wireOp",EDGE,"E127"),sQuery(id+"F0.wireOp",EDGE,"E128"),sQuery(id+"F0.wireOp",EDGE,"E129"),sQuery(id+"F0.wireOp",EDGE,"E130"),sQuery(id+"F0.wireOp",EDGE,"E131"),sQuery(id+"F0.wireOp",EDGE,"E132"),sQuery(id+"F0.wireOp",EDGE,"E133"),sQuery(id+"F0.wireOp",EDGE,"E134"),sQuery(id+"F0.wireOp",EDGE,"E135"),sQuery(id+"F0.wireOp",EDGE,"E136"),sQuery(id+"F0.wireOp",EDGE,"E137"),sQuery(id+"F0.wireOp",EDGE,"E138"),sQuery(id+"F0.wireOp",EDGE,"E139"),sQuery(id+"F0.wireOp",EDGE,"E140"),sQuery(id+"F0.wireOp",EDGE,"E141"),sQuery(id+"F0.wireOp",EDGE,"E142"),sQuery(id+"F0.wireOp",EDGE,"E143"),sQuery(id+"F0.wireOp",EDGE,"E144"),sQuery(id+"F0.wireOp",EDGE,"E145"),sQuery(id+"F0.wireOp",EDGE,"E146"),sQuery(id+"F0.wireOp",EDGE,"E147"),sQuery(id+"F0.wireOp",EDGE,"E148"),sQuery(id+"F0.wireOp",EDGE,"E149"),sQuery(id+"F0.wireOp",EDGE,"E150"),sQuery(id+"F0.wireOp",EDGE,"E151"),sQuery(id+"F0.wireOp",EDGE,"E152"),sQuery(id+"F0.wireOp",EDGE,"E156"),sQuery(id+"F0.wireOp",EDGE,"E157"),sQuery(id+"F0.wireOp",EDGE,"E158"),sQuery(id+"F0.wireOp",EDGE,"E159"),sQuery(id+"F0.wireOp",EDGE,"E160"),sQuery(id+"F0.wireOp",EDGE,"E161"),sQuery(id+"F0.wireOp",EDGE,"E162"),sQuery(id+"F0.wireOp",EDGE,"E163"),sQuery(id+"F0.wireOp",EDGE,"E164"),sQuery(id+"F0.wireOp",EDGE,"E165"),sQuery(id+"F0.wireOp",EDGE,"E166"),sQuery(id+"F0.wireOp",EDGE,"E167"),sQuery(id+"F0.wireOp",EDGE,"E168"),sQuery(id+"F0.wireOp",EDGE,"E169"),sQuery(id+"F0.wireOp",EDGE,"E170"),sQuery(id+"F0.wireOp",EDGE,"E171"),sQuery(id+"F0.wireOp",EDGE,"E172"),sQuery(id+"F0.wireOp",EDGE,"E173"),sQuery(id+"F0.wireOp",EDGE,"E174"),sQuery(id+"F0.wireOp",EDGE,"E175"),sQuery(id+"F0.wireOp",EDGE,"E176"),sQuery(id+"F0.wireOp",EDGE,"E177"),sQuery(id+"F0.wireOp",EDGE,"E178"),sQuery(id+"F0.wireOp",EDGE,"E179"),sQuery(id+"F0.wireOp",EDGE,"E182"),sQuery(id+"F0.wireOp",EDGE,"E183"),sQuery(id+"F0.wireOp",EDGE,"E184"),sQuery(id+"F0.wireOp",EDGE,"E185"),sQuery(id+"F0.wireOp",EDGE,"E186"),sQuery(id+"F0.wireOp",EDGE,"E187"),sQuery(id+"F0.wireOp",EDGE,"E188"),sQuery(id+"F0.wireOp",EDGE,"E189"),sQuery(id+"F0.wireOp",EDGE,"E190"),sQuery(id+"F0.wireOp",EDGE,"E191"),sQuery(id+"F0.wireOp",EDGE,"E192"),sQuery(id+"F0.wireOp",EDGE,"E193"),sQuery(id+"F0.wireOp",EDGE,"E194"),sQuery(id+"F0.wireOp",EDGE,"E195"),sQuery(id+"F0.wireOp",EDGE,"E196"),sQuery(id+"F0.wireOp",EDGE,"E197"),sQuery(id+"F0.wireOp",EDGE,"E198"),sQuery(id+"F0.wireOp",EDGE,"E199"),sQuery(id+"F0.wireOp",EDGE,"E200"),sQuery(id+"F0.wireOp",EDGE,"E201"),sQuery(id+"F0.wireOp",EDGE,"E202"),sQuery(id+"F0.wireOp",EDGE,"E203"),sQuery(id+"F0.wireOp",EDGE,"E204"),sQuery(id+"F0.wireOp",EDGE,"E205"),sQuery(id+"F0.wireOp",EDGE,"E206"),sQuery(id+"F0.wireOp",EDGE,"E207"),sQuery(id+"F0.wireOp",EDGE,"E208"),sQuery(id+"F0.wireOp",EDGE,"E209"),sQuery(id+"F0.wireOp",EDGE,"E210"),sQuery(id+"F0.wireOp",EDGE,"E211"),sQuery(id+"F0.wireOp",EDGE,"E212"),sQuery(id+"F0.wireOp",EDGE,"E213"),sQuery(id+"F0.wireOp",EDGE,"E214"),sQuery(id+"F0.wireOp",EDGE,"E215"),sQuery(id+"F0.wireOp",EDGE,"E216"),sQuery(id+"F0.wireOp",EDGE,"E217.bottom"),sQuery(id+"F0.wireOp",EDGE,"E217.top"),sQuery(id+"F0.wireOp",EDGE,"E217.left"),sQuery(id+"F0.wireOp",EDGE,"E217.right"),sQuery(id+"F0.wireOp",EDGE,"E218.bottom"),sQuery(id+"F0.wireOp",EDGE,"E218.top"),sQuery(id+"F0.wireOp",EDGE,"E218.left"),sQuery(id+"F0.wireOp",EDGE,"E219.bottom"),sQuery(id+"F0.wireOp",EDGE,"E219.top"),sQuery(id+"F0.wireOp",EDGE,"E219.left"),sQuery(id+"F0.wireOp",EDGE,"E220.bottom"),sQuery(id+"F0.wireOp",EDGE,"E220.top"),sQuery(id+"F0.wireOp",EDGE,"E220.left"),sQuery(id+"F0.wireOp",EDGE,"E221.trimOffspring"),sQuery(id+"F0.wireOp",EDGE,"E222.bottom"),sQuery(id+"F0.wireOp",EDGE,"E222.top"),sQuery(id+"F0.wireOp",EDGE,"E222.left"),sQuery(id+"F0.wireOp",EDGE,"E222.right"),sQuery(id+"F0.wireOp",EDGE,"E223.top"),sQuery(id+"F0.wireOp",EDGE,"E223.left"),sQuery(id+"F0.wireOp",EDGE,"E223.right"),sQuery(id+"F0.wireOp",EDGE,"E224.trimOffspring"),sQuery(id+"F0.wireOp",EDGE,"E225.bottom"),sQuery(id+"F0.wireOp",EDGE,"E225.left"),sQuery(id+"F0.wireOp",EDGE,"E225.right"),sQuery(id+"F0.wireOp",EDGE,"E226.bottom"),sQuery(id+"F0.wireOp",EDGE,"E226.left"),sQuery(id+"F0.wireOp",EDGE,"E226.right"),sQuery(id+"F0.wireOp",EDGE,"E227"),sQuery(id+"F0.wireOp",EDGE,"E228"),sQuery(id+"F0.wireOp",EDGE,"E229"),sQuery(id+"F0.wireOp",EDGE,"E230"),sQuery(id+"F0.wireOp",EDGE,"E231"),sQuery(id+"F0.wireOp",EDGE,"E232"),sQuery(id+"F0.wireOp",EDGE,"E233"),sQuery(id+"F0.wireOp",EDGE,"E234"),sQuery(id+"F0.wireOp",EDGE,"E235"),sQuery(id+"F0.wireOp",EDGE,"E236"),sQuery(id+"F0.wireOp",EDGE,"E237"),sQuery(id+"F0.wireOp",EDGE,"E238")])],"isStart":true});
            var sketch = newSketch(context, id + "F2", { "sketchPlane" : qUnion([Q0])});
            skLineSegment(sketch, "E239.bottom", {"start": v(-70.76, 48.04) * mm, "end": v(90.08, 48.04) * mm});
            skLineSegment(sketch, "E239.top", {"start": v(-70.76, 8.91) * mm, "end": v(90.08, 8.91) * mm});
            skLineSegment(sketch, "E239.left", {"start": v(-70.76, 48.04) * mm, "end": v(-70.76, 8.91) * mm});
            skLineSegment(sketch, "E239.right", {"start": v(90.08, 48.04) * mm, "end": v(90.08, 8.91) * mm});
            skSolve(sketch);
        }
        {
            var Q0;
            Q0 = qSketchRegion(id + "F2", true);
            extrude(context, id + "F3", {"entities" : qUnion([Q0]), "operationType" : NewBodyOperationType.ADD, "oppositeDirection" : true, "depth" : 31.75 * mm});
        }
        {
            var Q0;
            Q0=makeQuery(id+"F1.opExtrude","CAP_EDGE",EDGE,{"disambiguationData":[OSD([sQuery(id+"F0.wireOp",EDGE,"E7")])],"isStart":false});
            var Q1;
            Q1=makeQuery(id+"F1.opExtrude","CAP_EDGE",EDGE,{"disambiguationData":[OSD([sQuery(id+"F0.wireOp",EDGE,"E6")])],"isStart":false});
            var Q2;
            Q2=makeQuery(id+"F1.opExtrude","CAP_EDGE",EDGE,{"disambiguationData":[OSD([sQuery(id+"F0.wireOp",EDGE,"E5")])],"isStart":true});
            var Q3;
            Q3=makeQuery(id+"F1.opExtrude","SWEPT_EDGE",EDGE,{"disambiguationData":[OSD([sQuery(id+"F0.wireOp",EDGE,"E5"),sQuery(id+"F0.wireOp",EDGE,"E7")])]});
            var Q4;
            Q4=makeQuery(id+"F1.opExtrude","SWEPT_FACE",FACE,{"disambiguationData":[OSD([sQuery(id+"F0.wireOp",EDGE,"E5")])]});
            var Q5;
            Q5=makeQuery(id+"F1.opExtrude","CAP_EDGE",EDGE,{"disambiguationData":[OSD([sQuery(id+"F0.wireOp",EDGE,"E7")])],"isStart":true});
            var Q6;
            Q6=makeQuery(id+"F1.opExtrude","CAP_EDGE",EDGE,{"disambiguationData":[OSD([sQuery(id+"F0.wireOp",EDGE,"E6")])],"isStart":true});
            var Q7;
            Q7=makeQuery(id+"F1.opExtrude","SWEPT_FACE",FACE,{"disambiguationData":[OSD([sQuery(id+"F0.wireOp",EDGE,"E2")])]});
            fillet(context, id + "F4", {"entities" : qUnion([Q0, Q1, Q2, Q3, Q4, Q5, Q6, Q7]), "radius" : 5.08 * mm, "tangentPropagation" : true, "allowEdgeOverflow" : false});
        }
    });
